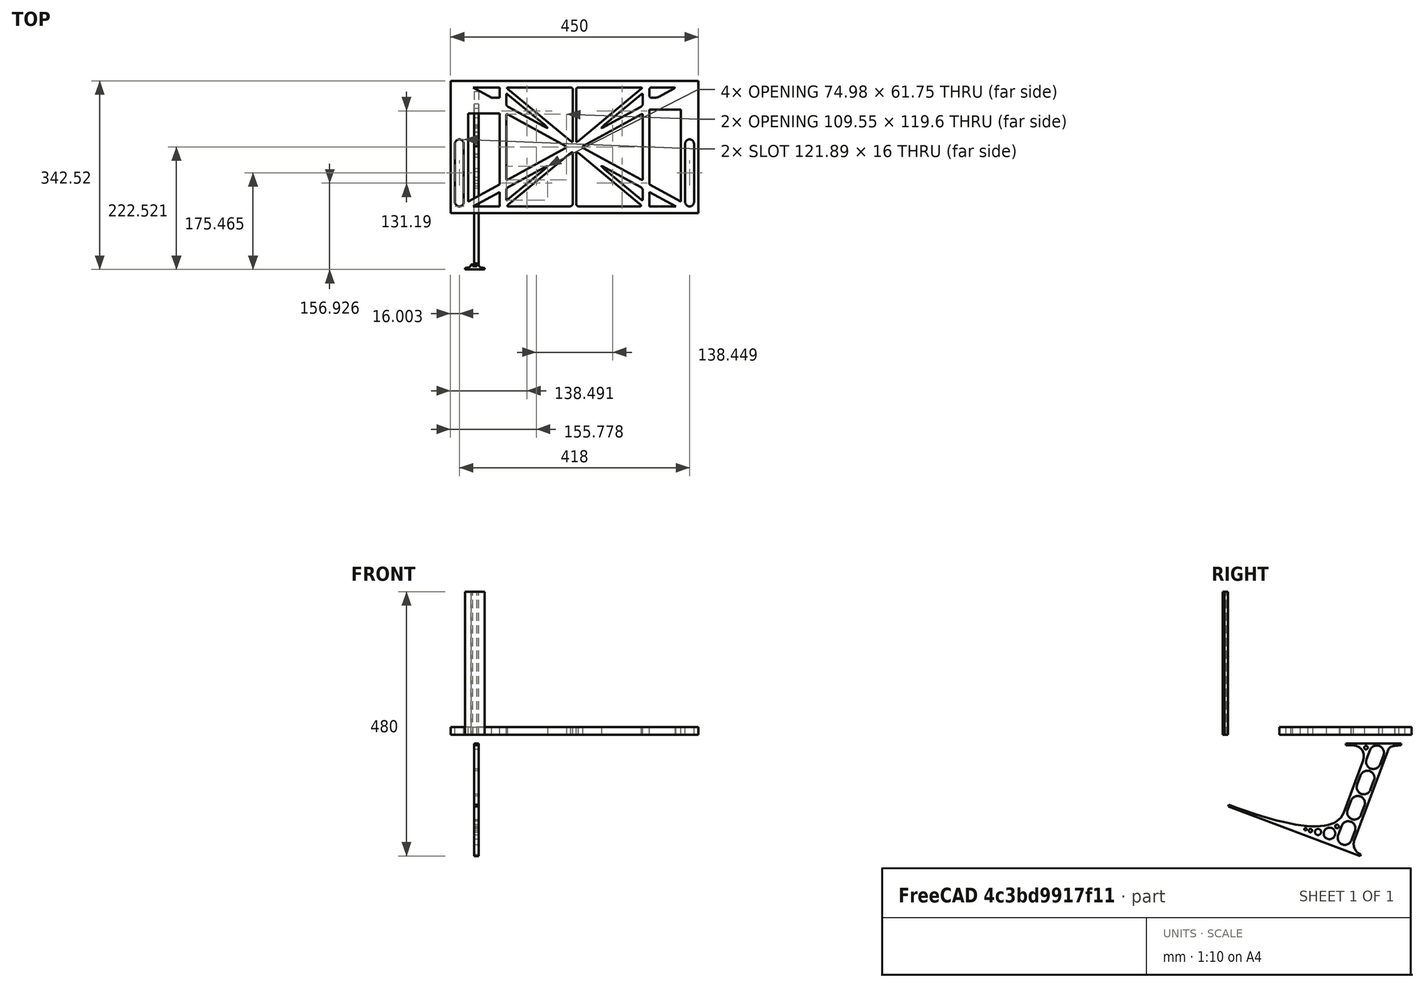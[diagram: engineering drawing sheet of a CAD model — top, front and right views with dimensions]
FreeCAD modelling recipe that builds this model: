
FCSTD DOCUMENT  (FreeCAD 0.19R0.19.2)
Label: laptopStand104
License: All rights reserved
LicenseURL: http://en.wikipedia.org/wiki/All_rights_reserved
objects: Sketcher::SketchObject×3, Part::Extrusion×3
note: 6 computed .brp shape members not serialized (recipe doc carries the construction recipe); baked Part::Feature solids carry a one-line shape summary decoded from their .brp

FEATURE [Sketcher::SketchObject] Sketch
  FullyConstrained = false
  sketch-geometry (294):
    g0: LineSegment StartX=-10.9272 StartY=-82.7794 StartZ=0 EndX=46.0728 EndY=-51.4823 EndZ=0
    g1: LineSegment StartX=366.073 StartY=-91.7794 StartZ=0 EndX=318.073 EndY=-65.424 EndZ=0
    g2: LineSegment StartX=-10.9272 StartY=77.3346 StartZ=0 EndX=-10.9272 EndY=-82.7794 EndZ=0
    g3: LineSegment StartX=375.073 StartY=-82.7896 StartZ=0 EndX=375.073 EndY=83.9235 EndZ=0
    g4: LineSegment StartX=-1.92719 StartY=-91.7794 StartZ=0 EndX=46.0728 EndY=-91.7794 EndZ=0
    g5: LineSegment StartX=318.073 StartY=83.9235 StartZ=0 EndX=318.073 EndY=-51.4823 EndZ=0
    g6: LineSegment StartX=318.073 StartY=-51.4823 StartZ=0 EndX=375.073 EndY=-82.7794 EndZ=0
    g7: LineSegment StartX=318.073 StartY=-65.424 StartZ=0 EndX=318.073 EndY=-91.7794 EndZ=0
    g8: LineSegment StartX=318.073 StartY=-91.7794 StartZ=0 EndX=366.073 EndY=-91.7794 EndZ=0
    g9: LineSegment StartX=46.0728 StartY=-65.424 StartZ=0 EndX=-1.92719 EndY=-91.7794 EndZ=0
    g10: LineSegment StartX=46.0728 StartY=-65.424 StartZ=0 EndX=46.0728 EndY=-91.7794 EndZ=0
    g11: LineSegment StartX=46.0728 StartY=77.3346 StartZ=0 EndX=46.0728 EndY=-51.4823 EndZ=0
    g12: LineSegment StartX=-42.9272 StartY=136.221 StartZ=0 EndX=-42.9272 EndY=-103.779 EndZ=0
    g13: LineSegment StartX=407.073 StartY=136.221 StartZ=0 EndX=407.073 EndY=-103.779 EndZ=0
    g14: ArcOfCircle CenterX=-26.9272 CenterY=22.1087 CenterZ=0 NormalX=0 NormalY=0 NormalZ=1 AngleXU=0 Radius=8 StartAngle=1e-16 EndAngle=3.14159
    g15: ArcOfCircle CenterX=-26.9272 CenterY=-83.7794 CenterZ=0 NormalX=0 NormalY=0 NormalZ=1 AngleXU=0 Radius=8 StartAngle=3.14159 EndAngle=6.28319
    g16: LineSegment StartX=-34.9272 StartY=22.1087 StartZ=0 EndX=-34.9272 EndY=-83.7794 EndZ=0
    g17: LineSegment StartX=-18.9272 StartY=22.1087 StartZ=0 EndX=-18.9272 EndY=-83.7794 EndZ=0
    g18: ArcOfCircle CenterX=391.073 CenterY=22.1087 CenterZ=0 NormalX=0 NormalY=0 NormalZ=1 AngleXU=0 Radius=8 StartAngle=-4.4e-15 EndAngle=3.14159
    g19: LineSegment StartX=399.073 StartY=22.1087 StartZ=0 EndX=399.073 EndY=-83.7794 EndZ=0
    g20: LineSegment StartX=383.073 StartY=22.1087 StartZ=0 EndX=383.073 EndY=-83.7794 EndZ=0
    g21: ArcOfCircle CenterX=391.073 CenterY=-83.7794 CenterZ=0 NormalX=0 NormalY=0 NormalZ=1 AngleXU=0 Radius=8 StartAngle=3.14159 EndAngle=6.28319
    g22: Circle CenterX=175.022 CenterY=27.0628 CenterZ=0 NormalX=0 NormalY=0 NormalZ=1 AngleXU=0 Radius=1
    g23: Circle CenterX=179.022 CenterY=24.8665 CenterZ=0 NormalX=0 NormalY=0 NormalZ=1 AngleXU=0 Radius=1
    g24: Circle CenterX=179.022 CenterY=27.0628 CenterZ=0 NormalX=0 NormalY=0 NormalZ=1 AngleXU=0 Radius=1
    g25: BSplineCurve PolesCount=3 KnotsCount=2 Degree=2 IsPeriodic=0
    g26: GeomPoint X=175.022 Y=27.0628 Z=0
    g27: GeomPoint X=179.022 Y=27.0628 Z=0
    g28: Circle CenterX=189.124 CenterY=27.0628 CenterZ=0 NormalX=0 NormalY=0 NormalZ=1 AngleXU=0 Radius=1
    g29: Circle CenterX=185.124 CenterY=24.8665 CenterZ=0 NormalX=0 NormalY=0 NormalZ=1 AngleXU=0 Radius=1
    g30: Circle CenterX=185.124 CenterY=27.0628 CenterZ=0 NormalX=0 NormalY=0 NormalZ=1 AngleXU=0 Radius=1
    g31: BSplineCurve PolesCount=3 KnotsCount=2 Degree=2 IsPeriodic=0
    g32: GeomPoint X=189.124 Y=27.0628 Z=0
    g33: GeomPoint X=185.124 Y=27.0628 Z=0
    g34: Circle CenterX=175.022 CenterY=5.37834 CenterZ=0 NormalX=0 NormalY=0 NormalZ=1 AngleXU=0 Radius=1
    g35: Circle CenterX=179.022 CenterY=7.57463 CenterZ=0 NormalX=0 NormalY=0 NormalZ=1 AngleXU=0 Radius=1
    g36: Circle CenterX=179.022 CenterY=5.34704 CenterZ=0 NormalX=0 NormalY=0 NormalZ=1 AngleXU=0 Radius=1
    g37: BSplineCurve PolesCount=3 KnotsCount=2 Degree=2 IsPeriodic=0
    g38: GeomPoint X=175.022 Y=5.37834 Z=0
    g39: GeomPoint X=179.022 Y=5.34704 Z=0
    g40: Circle CenterX=189.124 CenterY=5.37834 CenterZ=0 NormalX=0 NormalY=0 NormalZ=1 AngleXU=0 Radius=1
    g41: Circle CenterX=185.124 CenterY=7.57463 CenterZ=0 NormalX=0 NormalY=0 NormalZ=1 AngleXU=0 Radius=1
    g42: Circle CenterX=185.124 CenterY=5.34704 CenterZ=0 NormalX=0 NormalY=0 NormalZ=1 AngleXU=0 Radius=1
    g43: BSplineCurve PolesCount=3 KnotsCount=2 Degree=2 IsPeriodic=0
    g44: GeomPoint X=189.124 Y=5.37834 Z=0
    g45: GeomPoint X=185.124 Y=5.34704 Z=0
    g46: Circle CenterX=165.871 CenterY=18.1458 CenterZ=0 NormalX=0 NormalY=0 NormalZ=1 AngleXU=0 Radius=1
    g47: Circle CenterX=169.377 CenterY=16.2206 CenterZ=0 NormalX=0 NormalY=0 NormalZ=1 AngleXU=0 Radius=1
    g48: Circle CenterX=165.871 CenterY=14.2954 CenterZ=0 NormalX=0 NormalY=0 NormalZ=1 AngleXU=0 Radius=1
    g49: BSplineCurve PolesCount=3 KnotsCount=2 Degree=2 IsPeriodic=0
    g50: GeomPoint X=165.871 Y=18.1458 Z=0
    g51: GeomPoint X=165.871 Y=14.2954 Z=0
    g52: Circle CenterX=198.275 CenterY=18.1458 CenterZ=0 NormalX=0 NormalY=0 NormalZ=1 AngleXU=0 Radius=1
    g53: Circle CenterX=194.768 CenterY=16.2206 CenterZ=0 NormalX=0 NormalY=0 NormalZ=1 AngleXU=0 Radius=1
    g54: Circle CenterX=198.275 CenterY=14.2954 CenterZ=0 NormalX=0 NormalY=0 NormalZ=1 AngleXU=0 Radius=1
    g55: BSplineCurve PolesCount=3 KnotsCount=2 Degree=2 IsPeriodic=0
    g56: GeomPoint X=198.275 Y=18.1458 Z=0
    g57: GeomPoint X=198.275 Y=14.2954 Z=0
    g58: LineSegment StartX=407.073 StartY=-103.779 StartZ=0 EndX=-42.9272 EndY=-103.779 EndZ=0
    g59: LineSegment StartX=407.073 StartY=136.221 StartZ=0 EndX=-42.9272 EndY=136.221 EndZ=0
    g60: LineSegment StartX=46.0728 StartY=77.3346 StartZ=0 EndX=-10.9272 EndY=77.3346 EndZ=0
    g61: LineSegment StartX=46.0728 StartY=105.865 StartZ=0 EndX=31.5028 EndY=105.865 EndZ=0
    g62: LineSegment StartX=46.0728 StartY=124.221 StartZ=0 EndX=46.0728 EndY=105.865 EndZ=0
    g63: LineSegment StartX=-1.92719 StartY=124.221 StartZ=0 EndX=31.5028 EndY=105.865 EndZ=0
    g64: LineSegment StartX=46.0728 StartY=124.221 StartZ=0 EndX=-1.92719 EndY=124.221 EndZ=0
    g65: LineSegment StartX=318.073 StartY=83.9235 StartZ=0 EndX=375.073 EndY=83.9235 EndZ=0
    g66: Circle CenterX=125.607 CenterY=54.1951 CenterZ=0 NormalX=0 NormalY=0 NormalZ=1 AngleXU=0 Radius=1
    g67: Circle CenterX=139.632 CenterY=46.4944 CenterZ=0 NormalX=0 NormalY=0 NormalZ=1 AngleXU=0 Radius=1
    g68: Circle CenterX=127.326 CenterY=56.7187 CenterZ=0 NormalX=0 NormalY=0 NormalZ=1 AngleXU=0 Radius=1
    g69: BSplineCurve PolesCount=3 KnotsCount=2 Degree=2 IsPeriodic=0
    g70: GeomPoint X=125.607 Y=54.1951 Z=0
    g71: GeomPoint X=127.326 Y=56.7187 Z=0
    g72: Circle CenterX=236.821 CenterY=56.7187 CenterZ=0 NormalX=0 NormalY=0 NormalZ=1 AngleXU=0 Radius=1
    g73: Circle CenterX=224.513 CenterY=46.4944 CenterZ=0 NormalX=0 NormalY=0 NormalZ=1 AngleXU=0 Radius=1
    g74: Circle CenterX=238.538 CenterY=54.1951 CenterZ=0 NormalX=0 NormalY=0 NormalZ=1 AngleXU=0 Radius=1
    g75: BSplineCurve PolesCount=3 KnotsCount=2 Degree=2 IsPeriodic=0
    g76: GeomPoint X=236.821 Y=56.7187 Z=0
    g77: GeomPoint X=238.538 Y=54.1951 Z=0
    g78: Circle CenterX=238.538 CenterY=-21.7539 CenterZ=0 NormalX=0 NormalY=0 NormalZ=1 AngleXU=0 Radius=1
    g79: Circle CenterX=224.513 CenterY=-14.0532 CenterZ=0 NormalX=0 NormalY=0 NormalZ=1 AngleXU=0 Radius=1
    g80: Circle CenterX=236.821 CenterY=-24.2775 CenterZ=0 NormalX=0 NormalY=0 NormalZ=1 AngleXU=0 Radius=1
    g81: BSplineCurve PolesCount=3 KnotsCount=2 Degree=2 IsPeriodic=0
    g82: GeomPoint X=238.538 Y=-21.7539 Z=0
    g83: GeomPoint X=236.821 Y=-24.2775 Z=0
    g84: Circle CenterX=125.607 CenterY=-21.7539 CenterZ=0 NormalX=0 NormalY=0 NormalZ=1 AngleXU=0 Radius=1
    g85: Circle CenterX=139.632 CenterY=-14.0532 CenterZ=0 NormalX=0 NormalY=0 NormalZ=1 AngleXU=0 Radius=1
    g86: Circle CenterX=127.325 CenterY=-24.2775 CenterZ=0 NormalX=0 NormalY=0 NormalZ=1 AngleXU=0 Radius=1
    g87: BSplineCurve PolesCount=3 KnotsCount=2 Degree=2 IsPeriodic=0
    g88: GeomPoint X=125.607 Y=-21.7539 Z=0
    g89: GeomPoint X=127.325 Y=-24.2775 Z=0
    g90: Circle CenterX=302.996 CenterY=111.695 CenterZ=0 NormalX=0 NormalY=0 NormalZ=1 AngleXU=0 Radius=1
    g91: Circle CenterX=306.073 CenterY=114.251 CenterZ=0 NormalX=0 NormalY=0 NormalZ=1 AngleXU=0 Radius=1
    g92: Circle CenterX=306.073 CenterY=110.251 CenterZ=0 NormalX=0 NormalY=0 NormalZ=1 AngleXU=0 Radius=1
    g93: BSplineCurve PolesCount=3 KnotsCount=2 Degree=2 IsPeriodic=0
    g94: GeomPoint X=302.996 Y=111.695 Z=0
    g95: GeomPoint X=306.073 Y=110.251 Z=0
    g96: Circle CenterX=306.073 CenterY=95.2763 CenterZ=0 NormalX=0 NormalY=0 NormalZ=1 AngleXU=0 Radius=1
    g97: Circle CenterX=306.073 CenterY=91.2763 CenterZ=0 NormalX=0 NormalY=0 NormalZ=1 AngleXU=0 Radius=1
    g98: Circle CenterX=302.567 CenterY=89.3511 CenterZ=0 NormalX=0 NormalY=0 NormalZ=1 AngleXU=0 Radius=1
    g99: BSplineCurve PolesCount=3 KnotsCount=2 Degree=2 IsPeriodic=0
    g100: GeomPoint X=306.073 Y=95.2763 Z=0
    g101: GeomPoint X=302.567 Y=89.3511 Z=0
    g102: LineSegment StartX=306.073 StartY=110.251 StartZ=0 EndX=306.073 EndY=95.2763 EndZ=0
    g103: LineSegment StartX=302.996 StartY=111.695 StartZ=0 EndX=236.821 EndY=56.7187 EndZ=0
    g104: LineSegment StartX=238.538 StartY=54.1951 StartZ=0 EndX=302.567 EndY=89.3511 EndZ=0
    g105: Circle CenterX=61.1496 CenterY=111.695 CenterZ=0 NormalX=0 NormalY=0 NormalZ=1 AngleXU=0 Radius=1
    g106: Circle CenterX=58.0728 CenterY=114.251 CenterZ=0 NormalX=0 NormalY=0 NormalZ=1 AngleXU=0 Radius=1
    g107: Circle CenterX=58.0728 CenterY=110.251 CenterZ=0 NormalX=0 NormalY=0 NormalZ=1 AngleXU=0 Radius=1
    g108: BSplineCurve PolesCount=3 KnotsCount=2 Degree=2 IsPeriodic=0
    g109: GeomPoint X=61.1496 Y=111.695 Z=0
    g110: GeomPoint X=58.0728 Y=110.251 Z=0
    g111: Circle CenterX=61.5791 CenterY=89.3511 CenterZ=0 NormalX=0 NormalY=0 NormalZ=1 AngleXU=0 Radius=1
    g112: Circle CenterX=58.0728 CenterY=91.2763 CenterZ=0 NormalX=0 NormalY=0 NormalZ=1 AngleXU=0 Radius=1
    g113: Circle CenterX=58.0728 CenterY=95.2763 CenterZ=0 NormalX=0 NormalY=0 NormalZ=1 AngleXU=0 Radius=1
    g114: BSplineCurve PolesCount=3 KnotsCount=2 Degree=2 IsPeriodic=0
    g115: GeomPoint X=61.5791 Y=89.3511 Z=0
    g116: GeomPoint X=58.0728 Y=95.2763 Z=0
    g117: LineSegment StartX=58.0728 StartY=110.251 StartZ=0 EndX=58.0728 EndY=95.2763 EndZ=0
    g118: LineSegment StartX=61.1496 StartY=111.695 StartZ=0 EndX=127.326 EndY=56.7187 EndZ=0
    g119: LineSegment StartX=125.607 StartY=54.1951 StartZ=0 EndX=61.5791 EndY=89.3511 EndZ=0
    g120: Circle CenterX=61.5791 CenterY=-56.9099 CenterZ=0 NormalX=0 NormalY=0 NormalZ=1 AngleXU=0 Radius=1
    g121: Circle CenterX=58.0728 CenterY=-58.8351 CenterZ=0 NormalX=0 NormalY=0 NormalZ=1 AngleXU=0 Radius=1
    g122: Circle CenterX=58.0728 CenterY=-62.8351 CenterZ=0 NormalX=0 NormalY=0 NormalZ=1 AngleXU=0 Radius=1
    g123: BSplineCurve PolesCount=3 KnotsCount=2 Degree=2 IsPeriodic=0
    g124: GeomPoint X=61.5791 Y=-56.9099 Z=0
    g125: GeomPoint X=58.0728 Y=-62.8351 Z=0
    g126: Circle CenterX=58.0728 CenterY=-77.8102 CenterZ=0 NormalX=0 NormalY=0 NormalZ=1 AngleXU=0 Radius=1
    g127: Circle CenterX=58.0728 CenterY=-81.8102 CenterZ=0 NormalX=0 NormalY=0 NormalZ=1 AngleXU=0 Radius=1
    g128: Circle CenterX=61.1496 CenterY=-79.2541 CenterZ=0 NormalX=0 NormalY=0 NormalZ=1 AngleXU=0 Radius=1
    g129: BSplineCurve PolesCount=3 KnotsCount=2 Degree=2 IsPeriodic=0
    g130: GeomPoint X=58.0728 Y=-77.8102 Z=0
    g131: GeomPoint X=61.1496 Y=-79.2541 Z=0
    g132: LineSegment StartX=58.0728 StartY=-62.8351 StartZ=0 EndX=58.0728 EndY=-77.8102 EndZ=0
    g133: LineSegment StartX=61.1496 StartY=-79.2541 StartZ=0 EndX=127.325 EndY=-24.2775 EndZ=0
    g134: LineSegment StartX=125.607 StartY=-21.7539 StartZ=0 EndX=61.5791 EndY=-56.9099 EndZ=0
    g135: Circle CenterX=302.567 CenterY=-56.9099 CenterZ=0 NormalX=0 NormalY=0 NormalZ=1 AngleXU=0 Radius=1
    g136: Circle CenterX=306.073 CenterY=-58.8351 CenterZ=0 NormalX=0 NormalY=0 NormalZ=1 AngleXU=0 Radius=1
    g137: Circle CenterX=306.073 CenterY=-62.8351 CenterZ=0 NormalX=0 NormalY=0 NormalZ=1 AngleXU=0 Radius=1
    g138: BSplineCurve PolesCount=3 KnotsCount=2 Degree=2 IsPeriodic=0
    g139: GeomPoint X=302.567 Y=-56.9099 Z=0
    g140: GeomPoint X=306.073 Y=-62.8351 Z=0
    g141: Circle CenterX=302.996 CenterY=-79.2541 CenterZ=0 NormalX=0 NormalY=0 NormalZ=1 AngleXU=0 Radius=1
    g142: Circle CenterX=306.073 CenterY=-81.8102 CenterZ=0 NormalX=0 NormalY=0 NormalZ=1 AngleXU=0 Radius=1
    g143: Circle CenterX=306.073 CenterY=-77.8102 CenterZ=0 NormalX=0 NormalY=0 NormalZ=1 AngleXU=0 Radius=1
    g144: BSplineCurve PolesCount=3 KnotsCount=2 Degree=2 IsPeriodic=0
    g145: GeomPoint X=302.996 Y=-79.2541 Z=0
    g146: GeomPoint X=306.073 Y=-77.8102 Z=0
    g147: LineSegment StartX=306.073 StartY=-62.8351 StartZ=0 EndX=306.073 EndY=-77.8102 EndZ=0
    g148: LineSegment StartX=302.996 StartY=-79.2541 StartZ=0 EndX=236.821 EndY=-24.2775 EndZ=0
    g149: LineSegment StartX=238.538 StartY=-21.7539 StartZ=0 EndX=302.567 EndY=-56.9099 EndZ=0
    g150: Circle CenterX=61.6457 CenterY=-88.8112 CenterZ=0 NormalX=0 NormalY=0 NormalZ=1 AngleXU=0 Radius=1
    g151: Circle CenterX=58.0728 CenterY=-91.7794 CenterZ=0 NormalX=0 NormalY=0 NormalZ=1 AngleXU=0 Radius=1
    g152: Circle CenterX=63.9135 CenterY=-91.7794 CenterZ=0 NormalX=0 NormalY=0 NormalZ=1 AngleXU=0 Radius=1
    g153: BSplineCurve PolesCount=3 KnotsCount=2 Degree=2 IsPeriodic=0
    g154: GeomPoint X=61.6457 Y=-88.8112 Z=0
    g155: GeomPoint X=63.9135 Y=-91.7794 Z=0
    g156: Circle CenterX=179.022 CenterY=-85.8163 CenterZ=0 NormalX=0 NormalY=0 NormalZ=1 AngleXU=0 Radius=1
    g157: Circle CenterX=179.022 CenterY=-91.7794 CenterZ=0 NormalX=0 NormalY=0 NormalZ=1 AngleXU=0 Radius=1
    g158: Circle CenterX=171.895 CenterY=-91.7794 CenterZ=0 NormalX=0 NormalY=0 NormalZ=1 AngleXU=0 Radius=1
    g159: BSplineCurve PolesCount=3 KnotsCount=2 Degree=2 IsPeriodic=0
    g160: GeomPoint X=179.022 Y=-85.8163 Z=0
    g161: GeomPoint X=171.895 Y=-91.7794 Z=0
    g162: Circle CenterX=185.124 CenterY=-86.2028 CenterZ=0 NormalX=0 NormalY=0 NormalZ=1 AngleXU=0 Radius=1
    g163: Circle CenterX=185.124 CenterY=-91.7794 CenterZ=0 NormalX=0 NormalY=0 NormalZ=1 AngleXU=0 Radius=1
    g164: Circle CenterX=191.747 CenterY=-91.7794 CenterZ=0 NormalX=0 NormalY=0 NormalZ=1 AngleXU=0 Radius=1
    g165: BSplineCurve PolesCount=3 KnotsCount=2 Degree=2 IsPeriodic=0
    g166: GeomPoint X=185.124 Y=-86.2028 Z=0
    g167: GeomPoint X=191.747 Y=-91.7794 Z=0
    g168: Circle CenterX=299.888 CenterY=-86.6413 CenterZ=0 NormalX=0 NormalY=0 NormalZ=1 AngleXU=0 Radius=1
    g169: Circle CenterX=306.073 CenterY=-91.7794 CenterZ=0 NormalX=0 NormalY=0 NormalZ=1 AngleXU=0 Radius=1
    g170: Circle CenterX=298.776 CenterY=-91.7794 CenterZ=0 NormalX=0 NormalY=0 NormalZ=1 AngleXU=0 Radius=1
    g171: BSplineCurve PolesCount=3 KnotsCount=2 Degree=2 IsPeriodic=0
    g172: GeomPoint X=299.888 Y=-86.6413 Z=0
    g173: GeomPoint X=298.776 Y=-91.7794 Z=0
    g174: LineSegment StartX=189.124 StartY=5.37834 StartZ=0 EndX=299.888 EndY=-86.6413 EndZ=0
    g175: LineSegment StartX=298.776 StartY=-91.7794 StartZ=0 EndX=191.747 EndY=-91.7794 EndZ=0
    g176: LineSegment StartX=185.124 StartY=-86.2028 StartZ=0 EndX=185.124 EndY=5.34704 EndZ=0
    g177: LineSegment StartX=179.022 StartY=5.34704 StartZ=0 EndX=179.022 EndY=-85.8163 EndZ=0
    g178: LineSegment StartX=171.895 StartY=-91.7794 StartZ=0 EndX=63.9135 EndY=-91.7794 EndZ=0
    g179: LineSegment StartX=61.6457 StartY=-88.8112 StartZ=0 EndX=175.022 EndY=5.37834 EndZ=0
    g180: Circle CenterX=302.073 CenterY=124.221 CenterZ=0 NormalX=0 NormalY=0 NormalZ=1 AngleXU=0 Radius=1
    g181: Circle CenterX=306.073 CenterY=124.221 CenterZ=0 NormalX=0 NormalY=0 NormalZ=1 AngleXU=0 Radius=1
    g182: Circle CenterX=302.996 CenterY=121.665 CenterZ=0 NormalX=0 NormalY=0 NormalZ=1 AngleXU=0 Radius=1
    g183: BSplineCurve PolesCount=3 KnotsCount=2 Degree=2 IsPeriodic=0
    g184: GeomPoint X=302.073 Y=124.221 Z=0
    g185: GeomPoint X=302.996 Y=121.665 Z=0
    g186: Circle CenterX=189.124 CenterY=124.221 CenterZ=0 NormalX=0 NormalY=0 NormalZ=1 AngleXU=0 Radius=1
    g187: Circle CenterX=185.124 CenterY=124.221 CenterZ=0 NormalX=0 NormalY=0 NormalZ=1 AngleXU=0 Radius=1
    g188: Circle CenterX=185.124 CenterY=120.221 CenterZ=0 NormalX=0 NormalY=0 NormalZ=1 AngleXU=0 Radius=1
    g189: BSplineCurve PolesCount=3 KnotsCount=2 Degree=2 IsPeriodic=0
    g190: GeomPoint X=189.124 Y=124.221 Z=0
    g191: GeomPoint X=185.124 Y=120.221 Z=0
    g192: Circle CenterX=175.022 CenterY=124.221 CenterZ=0 NormalX=0 NormalY=0 NormalZ=1 AngleXU=0 Radius=1
    g193: Circle CenterX=179.022 CenterY=124.221 CenterZ=0 NormalX=0 NormalY=0 NormalZ=1 AngleXU=0 Radius=1
    g194: Circle CenterX=179.022 CenterY=120.221 CenterZ=0 NormalX=0 NormalY=0 NormalZ=1 AngleXU=0 Radius=1
    g195: BSplineCurve PolesCount=3 KnotsCount=2 Degree=2 IsPeriodic=0
    g196: GeomPoint X=175.022 Y=124.221 Z=0
    g197: GeomPoint X=179.022 Y=120.221 Z=0
    g198: Circle CenterX=62.0728 CenterY=124.221 CenterZ=0 NormalX=0 NormalY=0 NormalZ=1 AngleXU=0 Radius=1
    g199: Circle CenterX=58.0728 CenterY=124.221 CenterZ=0 NormalX=0 NormalY=0 NormalZ=1 AngleXU=0 Radius=1
    g200: Circle CenterX=61.1496 CenterY=121.665 CenterZ=0 NormalX=0 NormalY=0 NormalZ=1 AngleXU=0 Radius=1
    g201: BSplineCurve PolesCount=3 KnotsCount=2 Degree=2 IsPeriodic=0
    g202: GeomPoint X=62.0728 Y=124.221 Z=0
    g203: GeomPoint X=61.1496 Y=121.665 Z=0
    g204: LineSegment StartX=62.0728 StartY=124.221 StartZ=0 EndX=175.022 EndY=124.221 EndZ=0
    g205: LineSegment StartX=179.022 StartY=120.221 StartZ=0 EndX=179.022 EndY=27.0628 EndZ=0
    g206: LineSegment StartX=185.124 StartY=27.0628 StartZ=0 EndX=185.124 EndY=120.221 EndZ=0
    g207: LineSegment StartX=189.124 StartY=124.221 StartZ=0 EndX=302.073 EndY=124.221 EndZ=0
    g208: LineSegment StartX=302.996 StartY=121.665 StartZ=0 EndX=189.124 EndY=27.0628 EndZ=0
    g209: LineSegment StartX=175.022 StartY=27.0628 StartZ=0 EndX=61.1496 EndY=121.665 EndZ=0
    g210: Circle CenterX=61.5791 CenterY=75.4095 CenterZ=0 NormalX=0 NormalY=0 NormalZ=1 AngleXU=0 Radius=1
    g211: Circle CenterX=58.0728 CenterY=77.3346 CenterZ=0 NormalX=0 NormalY=0 NormalZ=1 AngleXU=0 Radius=1
    g212: Circle CenterX=58.0728 CenterY=73.3346 CenterZ=0 NormalX=0 NormalY=0 NormalZ=1 AngleXU=0 Radius=1
    g213: BSplineCurve PolesCount=3 KnotsCount=2 Degree=2 IsPeriodic=0
    g214: GeomPoint X=61.5791 Y=75.4095 Z=0
    g215: GeomPoint X=58.0728 Y=73.3346 Z=0
    g216: Circle CenterX=58.0728 CenterY=-40.8935 CenterZ=0 NormalX=0 NormalY=0 NormalZ=1 AngleXU=0 Radius=1
    g217: Circle CenterX=58.0728 CenterY=-44.8935 CenterZ=0 NormalX=0 NormalY=0 NormalZ=1 AngleXU=0 Radius=1
    g218: Circle CenterX=61.5791 CenterY=-42.9683 CenterZ=0 NormalX=0 NormalY=0 NormalZ=1 AngleXU=0 Radius=1
    g219: BSplineCurve PolesCount=3 KnotsCount=2 Degree=2 IsPeriodic=0
    g220: GeomPoint X=58.0728 Y=-40.8935 Z=0
    g221: GeomPoint X=61.5791 Y=-42.9683 Z=0
    g222: LineSegment StartX=61.5791 StartY=-42.9683 StartZ=0 EndX=165.871 EndY=14.2954 EndZ=0
    g223: LineSegment StartX=165.871 StartY=18.1458 StartZ=0 EndX=61.5791 EndY=75.4095 EndZ=0
    g224: LineSegment StartX=58.0728 StartY=73.3346 StartZ=0 EndX=58.0728 EndY=-40.8935 EndZ=0
    g225: Circle CenterX=302.567 CenterY=-42.9683 CenterZ=0 NormalX=0 NormalY=0 NormalZ=1 AngleXU=0 Radius=1
    g226: Circle CenterX=306.073 CenterY=-44.8935 CenterZ=0 NormalX=0 NormalY=0 NormalZ=1 AngleXU=0 Radius=1
    g227: Circle CenterX=306.073 CenterY=-40.8935 CenterZ=0 NormalX=0 NormalY=0 NormalZ=1 AngleXU=0 Radius=1
    g228: BSplineCurve PolesCount=3 KnotsCount=2 Degree=2 IsPeriodic=0
    g229: GeomPoint X=302.567 Y=-42.9683 Z=0
    g230: GeomPoint X=306.073 Y=-40.8935 Z=0
    g231: Circle CenterX=306.073 CenterY=73.3346 CenterZ=0 NormalX=0 NormalY=0 NormalZ=1 AngleXU=0 Radius=1
    g232: Circle CenterX=306.073 CenterY=77.3346 CenterZ=0 NormalX=0 NormalY=0 NormalZ=1 AngleXU=0 Radius=1
    g233: Circle CenterX=302.567 CenterY=75.4095 CenterZ=0 NormalX=0 NormalY=0 NormalZ=1 AngleXU=0 Radius=1
    g234: BSplineCurve PolesCount=3 KnotsCount=2 Degree=2 IsPeriodic=0
    g235: GeomPoint X=306.073 Y=73.3346 Z=0
    g236: GeomPoint X=302.567 Y=75.4095 Z=0
    g237: LineSegment StartX=302.567 StartY=-42.9683 StartZ=0 EndX=198.275 EndY=14.2954 EndZ=0
    g238: LineSegment StartX=198.275 StartY=18.1458 StartZ=0 EndX=302.567 EndY=75.4095 EndZ=0
    g239: LineSegment StartX=306.073 StartY=73.3346 StartZ=0 EndX=306.073 EndY=-40.8935 EndZ=0
    g240: LineSegment StartX=322.073 StartY=105.865 StartZ=0 EndX=328.643 EndY=105.865 EndZ=0
    g241: LineSegment StartX=318.073 StartY=120.221 StartZ=0 EndX=318.073 EndY=109.865 EndZ=0
    g242: LineSegment StartX=336.157 StartY=107.779 StartZ=0 EndX=362.567 EndY=122.294 EndZ=0
    g243: Circle CenterX=362.073 CenterY=124.221 CenterZ=0 NormalX=0 NormalY=0 NormalZ=1 AngleXU=0 Radius=1
    g244: Circle CenterX=366.073 CenterY=124.221 CenterZ=0 NormalX=0 NormalY=0 NormalZ=1 AngleXU=0 Radius=1
    g245: Circle CenterX=362.567 CenterY=122.294 CenterZ=0 NormalX=0 NormalY=0 NormalZ=1 AngleXU=0 Radius=1
    g246: BSplineCurve PolesCount=3 KnotsCount=2 Degree=2 IsPeriodic=0
    g247: GeomPoint X=362.073 Y=124.221 Z=0
    g248: GeomPoint X=362.567 Y=122.294 Z=0
    g249: Circle CenterX=322.073 CenterY=124.221 CenterZ=0 NormalX=0 NormalY=0 NormalZ=1 AngleXU=0 Radius=1
    g250: Circle CenterX=318.073 CenterY=124.221 CenterZ=0 NormalX=0 NormalY=0 NormalZ=1 AngleXU=0 Radius=1
    g251: Circle CenterX=318.073 CenterY=120.221 CenterZ=0 NormalX=0 NormalY=0 NormalZ=1 AngleXU=0 Radius=1
    g252: BSplineCurve PolesCount=3 KnotsCount=2 Degree=2 IsPeriodic=0
    g253: GeomPoint X=322.073 Y=124.221 Z=0
    g254: GeomPoint X=318.073 Y=120.221 Z=0
    g255: Circle CenterX=322.073 CenterY=105.865 CenterZ=0 NormalX=0 NormalY=0 NormalZ=1 AngleXU=0 Radius=1
    g256: Circle CenterX=318.073 CenterY=105.865 CenterZ=0 NormalX=0 NormalY=0 NormalZ=1 AngleXU=0 Radius=1
    g257: Circle CenterX=318.073 CenterY=109.865 CenterZ=0 NormalX=0 NormalY=0 NormalZ=1 AngleXU=0 Radius=1
    g258: BSplineCurve PolesCount=3 KnotsCount=2 Degree=2 IsPeriodic=0
    g259: GeomPoint X=322.073 Y=105.865 Z=0
    g260: GeomPoint X=318.073 Y=109.865 Z=0
    g261: Circle CenterX=336.157 CenterY=107.779 CenterZ=0 NormalX=0 NormalY=0 NormalZ=1 AngleXU=0 Radius=1
    g262: Circle CenterX=332.651 CenterY=105.853 CenterZ=0 NormalX=0 NormalY=0 NormalZ=1 AngleXU=0 Radius=1
    g263: Circle CenterX=328.643 CenterY=105.865 CenterZ=0 NormalX=0 NormalY=0 NormalZ=1 AngleXU=0 Radius=1
    g264: BSplineCurve PolesCount=3 KnotsCount=2 Degree=2 IsPeriodic=0
    g265: GeomPoint X=336.157 Y=107.779 Z=0
    g266: GeomPoint X=328.643 Y=105.865 Z=0
    g267: LineSegment StartX=322.073 StartY=124.221 StartZ=0 EndX=362.073 EndY=124.221 EndZ=0
    g268: LineSegment StartX=318.073 StartY=83.9235 StartZ=0 EndX=322.073 EndY=83.9235 EndZ=0
    g269: LineSegment StartX=318.073 StartY=83.9235 StartZ=0 EndX=318.073 EndY=79.9235 EndZ=0
    g270: LineSegment StartX=375.073 StartY=83.9235 StartZ=0 EndX=371.073 EndY=83.9235 EndZ=0
    g271: LineSegment StartX=375.073 StartY=83.9235 StartZ=0 EndX=375.073 EndY=79.9235 EndZ=0
    g272: LineSegment StartX=375.073 StartY=-82.7896 StartZ=0 EndX=375.073 EndY=-78.7896 EndZ=0
    g273: LineSegment StartX=318.073 StartY=-51.4823 StartZ=0 EndX=321.579 EndY=-53.4075 EndZ=0
    g274: LineSegment StartX=318.073 StartY=-51.4823 StartZ=0 EndX=318.073 EndY=-47.4823 EndZ=0
    g275: LineSegment StartX=375.073 StartY=-82.7896 StartZ=0 EndX=371.567 EndY=-80.8644 EndZ=0
    g276: Circle CenterX=371.567 CenterY=-80.8644 CenterZ=0 NormalX=0 NormalY=0 NormalZ=1 AngleXU=0 Radius=1
    g277: Circle CenterX=375.073 CenterY=-82.7896 CenterZ=0 NormalX=0 NormalY=0 NormalZ=1 AngleXU=0 Radius=1
    g278: Circle CenterX=375.073 CenterY=-78.7896 CenterZ=0 NormalX=0 NormalY=0 NormalZ=1 AngleXU=0 Radius=1
    g279: BSplineCurve PolesCount=3 KnotsCount=2 Degree=2 IsPeriodic=0
    g280: GeomPoint X=371.567 Y=-80.8644 Z=0
    g281: GeomPoint X=375.073 Y=-78.7896 Z=0
    g282: Circle CenterX=321.579 CenterY=-53.4075 CenterZ=0 NormalX=0 NormalY=0 NormalZ=1 AngleXU=0 Radius=1
    g283: Circle CenterX=318.073 CenterY=-51.4823 CenterZ=0 NormalX=0 NormalY=0 NormalZ=1 AngleXU=0 Radius=1
    g284: Circle CenterX=318.073 CenterY=-47.4823 CenterZ=0 NormalX=0 NormalY=0 NormalZ=1 AngleXU=0 Radius=1
    g285: BSplineCurve PolesCount=3 KnotsCount=2 Degree=2 IsPeriodic=0
    g286: GeomPoint X=321.579 Y=-53.4075 Z=0
    g287: GeomPoint X=318.073 Y=-47.4823 Z=0
    g288: Circle CenterX=318.073 CenterY=79.9235 CenterZ=0 NormalX=0 NormalY=0 NormalZ=1 AngleXU=0 Radius=1
    g289: Circle CenterX=318.073 CenterY=83.9235 CenterZ=0 NormalX=0 NormalY=0 NormalZ=1 AngleXU=0 Radius=1
    g290: Circle CenterX=322.073 CenterY=83.9235 CenterZ=0 NormalX=0 NormalY=0 NormalZ=1 AngleXU=0 Radius=1
    g291: BSplineCurve PolesCount=3 KnotsCount=2 Degree=2 IsPeriodic=0
    g292: GeomPoint X=318.073 Y=79.9235 Z=0
    g293: GeomPoint X=322.073 Y=83.9235 Z=0
  constraints (507):
    c: Horizontal(g4)
    c: Coincident(g5,g6)
    c: Coincident(g7,g1)
    c: Tangent(g5,g7)
    c: Coincident(g10,g9)
    c: Coincident(g0,g11)
    c: Block(g6)
    c: Block(g3)
    c: Block(g1)
    c: Block(g7)
    c: Block(g10)
    c: Block(g9)
    c: Block(g0)
    c: Block(g2)
    c: Block(g8)
    c: Block(g4)
    c: Vertical(g12)
    c: Vertical(g13)
    c: Block(g13)
    c: Block(g12)
    c: Tangent(g14,g17) = 1.5708
    c: Tangent(g14,g16) = -1.5708
    c: Tangent(g16,g15) = -1.5708
    c: Tangent(g17,g15) = 1.5708
    c: Vertical(g16)
    c: Equal(g14,g15)
    c: Block(g17)
    c: Block(g16)
    c: Tangent(g18,g19) = 1.5708
    c: Tangent(g19,g21) = 1.5708
    c: Equal(g18,g21)
    c: Coincident(g20,g18)
    c: Coincident(g20,g21)
    c: Block(g19)
    c: Block(g20)
    c: Weight(g22) = 1
    c: Equal(g22,g23)
    c: Equal(g22,g24)
    c: InternalAlignment(g22,g25)
    c: InternalAlignment(g23,g25)
    c: InternalAlignment(g24,g25)
    c: InternalAlignment(g26,g25)
    c: InternalAlignment(g27,g25)
    c: Weight(g28) = 1
    c: Equal(g28,g29)
    c: Equal(g28,g30)
    c: InternalAlignment(g28,g31)
    c: InternalAlignment(g29,g31)
    c: InternalAlignment(g30,g31)
    c: InternalAlignment(g32,g31)
    c: InternalAlignment(g33,g31)
    c: Block(g31)
    c: Block(g25)
    c: Weight(g34) = 1
    c: Equal(g34,g35)
    c: Equal(g34,g36)
    c: InternalAlignment(g34,g37)
    c: InternalAlignment(g35,g37)
    c: InternalAlignment(g36,g37)
    c: InternalAlignment(g38,g37)
    c: InternalAlignment(g39,g37)
    c: Weight(g40) = 1
    c: Equal(g40,g41)
    c: Equal(g40,g42)
    c: InternalAlignment(g40,g43)
    c: InternalAlignment(g41,g43)
    c: InternalAlignment(g42,g43)
    c: InternalAlignment(g44,g43)
    c: InternalAlignment(g45,g43)
    c: Block(g43)
    c: Block(g37)
    c: Weight(g46) = 1
    c: Equal(g46,g47)
    c: Equal(g46,g48)
    c: InternalAlignment(g46,g49)
    c: InternalAlignment(g47,g49)
    c: InternalAlignment(g48,g49)
    c: InternalAlignment(g50,g49)
    c: InternalAlignment(g51,g49)
    c: Weight(g52) = 1
    c: Equal(g52,g53)
    c: Equal(g52,g54)
    c: InternalAlignment(g52,g55)
    c: InternalAlignment(g53,g55)
    c: InternalAlignment(g54,g55)
    c: InternalAlignment(g56,g55)
    c: InternalAlignment(g57,g55)
    c: Block(g49)
    c: Block(g55)
    c: Coincident(g58,g13)
    c: Coincident(g58,g12)
    c: Horizontal(g58)
    c: Distance(g58) = 450
    c: Coincident(g59,g13)
    c: Coincident(g59,g12)
    c: Horizontal(g59)
    c: Horizontal(g60)
    c: Coincident(g11,g60)
    c: Horizontal(g61)
    c: Vertical(g62)
    c: Block(g62)
    c: Block(g61)
    c: Block(g60)
    c: Distance(g62) = 18.3554
    c: Coincident(g64,g62)
    c: Coincident(g64,g63)
    c: Horizontal(g64)
    c: Block(g64)
    c: Block(g63)
    c: Coincident(g61,g63)
    c: Coincident(g2,g60)
    c: Coincident(g65,g5)
    c: Horizontal(g65)
    c: Block(g65)
    c: Coincident(g3,g65)
    c: Weight(g66) = 1
    c: Equal(g66,g67)
    c: Equal(g66,g68)
    c: InternalAlignment(g66,g69)
    c: InternalAlignment(g67,g69)
    c: InternalAlignment(g68,g69)
    c: InternalAlignment(g70,g69)
    c: InternalAlignment(g71,g69)
    c: Block(g69)
    c: Weight(g72) = 1
    c: Equal(g72,g73)
    c: Equal(g72,g74)
    c: InternalAlignment(g72,g75)
    c: InternalAlignment(g73,g75)
    c: InternalAlignment(g74,g75)
    c: InternalAlignment(g76,g75)
    c: InternalAlignment(g77,g75)
    c: Block(g75)
    c: Weight(g78) = 1
    c: Equal(g78,g79)
    c: Equal(g78,g80)
    c: InternalAlignment(g78,g81)
    c: InternalAlignment(g79,g81)
    c: InternalAlignment(g80,g81)
    c: InternalAlignment(g82,g81)
    c: InternalAlignment(g83,g81)
    c: Block(g81)
    c: Weight(g84) = 1
    c: Equal(g84,g85)
    c: Equal(g84,g86)
    c: InternalAlignment(g84,g87)
    c: InternalAlignment(g85,g87)
    c: InternalAlignment(g86,g87)
    c: InternalAlignment(g88,g87)
    c: InternalAlignment(g89,g87)
    c: Block(g87)
    c: Weight(g90) = 1
    c: Equal(g90,g91)
    c: Equal(g90,g92)
    c: InternalAlignment(g90,g93)
    c: InternalAlignment(g91,g93)
    c: InternalAlignment(g92,g93)
    c: InternalAlignment(g94,g93)
    c: InternalAlignment(g95,g93)
    c: Weight(g96) = 1
    c: Equal(g96,g97)
    c: Equal(g96,g98)
    c: InternalAlignment(g96,g99)
    c: InternalAlignment(g97,g99)
    c: InternalAlignment(g98,g99)
    c: InternalAlignment(g100,g99)
    c: InternalAlignment(g101,g99)
    c: Block(g93)
    c: Block(g99)
    c: Coincident(g102,g93)
    c: Coincident(g102,g99)
    c: Vertical(g102)
    c: Coincident(g103,g93)
    c: Coincident(g103,g75)
    c: Coincident(g104,g75)
    c: Coincident(g104,g99)
    c: Weight(g105) = 1
    c: Equal(g105,g106)
    c: Equal(g105,g107)
    c: InternalAlignment(g105,g108)
    c: InternalAlignment(g106,g108)
    c: InternalAlignment(g107,g108)
    c: InternalAlignment(g109,g108)
    c: InternalAlignment(g110,g108)
    c: Weight(g111) = 1
    c: Equal(g111,g112)
    c: Equal(g111,g113)
    c: InternalAlignment(g111,g114)
    c: InternalAlignment(g112,g114)
    c: InternalAlignment(g113,g114)
    c: InternalAlignment(g115,g114)
    c: InternalAlignment(g116,g114)
    c: Block(g108)
    c: Block(g114)
    c: Coincident(g117,g108)
    c: Coincident(g117,g114)
    c: Vertical(g117)
    c: Coincident(g118,g108)
    c: Coincident(g118,g69)
    c: Coincident(g119,g69)
    c: Coincident(g119,g114)
    c: Weight(g120) = 1
    c: Equal(g120,g121)
    c: Equal(g120,g122)
    c: InternalAlignment(g120,g123)
    c: InternalAlignment(g121,g123)
    c: InternalAlignment(g122,g123)
    c: InternalAlignment(g124,g123)
    c: InternalAlignment(g125,g123)
    c: Weight(g126) = 1
    c: Equal(g126,g127)
    c: Equal(g126,g128)
    c: InternalAlignment(g126,g129)
    c: InternalAlignment(g127,g129)
    c: InternalAlignment(g128,g129)
    c: InternalAlignment(g130,g129)
    c: InternalAlignment(g131,g129)
    c: Block(g123)
    c: Block(g129)
    c: Coincident(g132,g123)
    c: Coincident(g132,g129)
    c: Vertical(g132)
    c: Coincident(g133,g129)
    c: Coincident(g133,g87)
    c: Coincident(g134,g87)
    c: Coincident(g134,g123)
    c: Weight(g135) = 1
    c: Equal(g135,g136)
    c: Equal(g135,g137)
    c: InternalAlignment(g135,g138)
    c: InternalAlignment(g136,g138)
    c: InternalAlignment(g137,g138)
    c: InternalAlignment(g139,g138)
    c: InternalAlignment(g140,g138)
    c: Weight(g141) = 1
    c: Equal(g141,g142)
    c: Equal(g141,g143)
    c: InternalAlignment(g141,g144)
    c: InternalAlignment(g142,g144)
    c: InternalAlignment(g143,g144)
    c: InternalAlignment(g145,g144)
    c: InternalAlignment(g146,g144)
    c: Block(g138)
    c: Block(g144)
    c: Coincident(g147,g138)
    c: Coincident(g147,g144)
    c: Vertical(g147)
    c: Coincident(g148,g144)
    c: Coincident(g148,g81)
    c: Coincident(g149,g81)
    c: Coincident(g149,g138)
    c: Weight(g150) = 1
    c: Equal(g150,g151)
    c: Equal(g150,g152)
    c: InternalAlignment(g150,g153)
    c: InternalAlignment(g151,g153)
    c: InternalAlignment(g152,g153)
    c: InternalAlignment(g154,g153)
    c: InternalAlignment(g155,g153)
    c: Weight(g156) = 1
    c: Equal(g156,g157)
    c: Equal(g156,g158)
    c: InternalAlignment(g156,g159)
    c: InternalAlignment(g157,g159)
    c: InternalAlignment(g158,g159)
    c: InternalAlignment(g160,g159)
    c: InternalAlignment(g161,g159)
    c: Weight(g162) = 1
    c: Equal(g162,g163)
    c: Equal(g162,g164)
    c: InternalAlignment(g162,g165)
    c: InternalAlignment(g163,g165)
    c: InternalAlignment(g164,g165)
    c: InternalAlignment(g166,g165)
    c: InternalAlignment(g167,g165)
    c: Weight(g168) = 1
    c: Equal(g168,g169)
    c: Equal(g168,g170)
    c: InternalAlignment(g168,g171)
    c: InternalAlignment(g169,g171)
    c: InternalAlignment(g170,g171)
    c: InternalAlignment(g172,g171)
    c: InternalAlignment(g173,g171)
    c: Block(g171)
    c: Block(g165)
    c: Block(g159)
    c: Block(g153)
    c: Coincident(g174,g43)
    c: Coincident(g174,g171)
    c: Coincident(g175,g171)
    c: Coincident(g175,g165)
    c: Horizontal(g175)
    c: Coincident(g176,g165)
    c: Coincident(g176,g43)
    c: Vertical(g176)
    c: Coincident(g177,g37)
    c: Coincident(g177,g159)
    c: Vertical(g177)
    c: Coincident(g178,g159)
    c: Coincident(g178,g153)
    c: Horizontal(g178)
    c: Coincident(g179,g153)
    c: Coincident(g179,g37)
    c: Weight(g180) = 1
    c: Equal(g180,g181)
    c: Equal(g180,g182)
    c: InternalAlignment(g180,g183)
    c: InternalAlignment(g181,g183)
    c: InternalAlignment(g182,g183)
    c: InternalAlignment(g184,g183)
    c: InternalAlignment(g185,g183)
    c: Weight(g186) = 1
    c: Equal(g186,g187)
    c: Equal(g186,g188)
    c: InternalAlignment(g186,g189)
    c: InternalAlignment(g187,g189)
    c: InternalAlignment(g188,g189)
    c: InternalAlignment(g190,g189)
    c: InternalAlignment(g191,g189)
    c: Weight(g192) = 1
    c: Equal(g192,g193)
    c: Equal(g192,g194)
    c: InternalAlignment(g192,g195)
    c: InternalAlignment(g193,g195)
    c: InternalAlignment(g194,g195)
    c: InternalAlignment(g196,g195)
    c: InternalAlignment(g197,g195)
    c: Weight(g198) = 1
    c: Equal(g198,g199)
    c: Equal(g198,g200)
    c: InternalAlignment(g198,g201)
    c: InternalAlignment(g199,g201)
    c: InternalAlignment(g200,g201)
    c: InternalAlignment(g202,g201)
    c: InternalAlignment(g203,g201)
    c: Block(g201)
    c: Block(g195)
    c: Block(g189)
    c: Block(g183)
    c: Coincident(g204,g201)
    c: Coincident(g204,g195)
    c: Horizontal(g204)
    c: Coincident(g205,g195)
    c: Coincident(g205,g25)
    c: Vertical(g205)
    c: Coincident(g206,g31)
    c: Coincident(g206,g189)
    c: Vertical(g206)
    c: Coincident(g207,g189)
    c: Coincident(g207,g183)
    c: Horizontal(g207)
    c: Coincident(g208,g183)
    c: Coincident(g208,g31)
    c: Coincident(g209,g25)
    c: Weight(g210) = 1
    c: Equal(g210,g211)
    c: Equal(g210,g212)
    c: InternalAlignment(g210,g213)
    c: InternalAlignment(g211,g213)
    c: InternalAlignment(g212,g213)
    c: InternalAlignment(g214,g213)
    c: InternalAlignment(g215,g213)
    c: Weight(g216) = 1
    c: Equal(g216,g217)
    c: Equal(g216,g218)
    c: InternalAlignment(g216,g219)
    c: InternalAlignment(g217,g219)
    c: InternalAlignment(g218,g219)
    c: InternalAlignment(g220,g219)
    c: InternalAlignment(g221,g219)
    c: Block(g219)
    c: Block(g213)
    c: Coincident(g222,g219)
    c: Coincident(g222,g49)
    c: Coincident(g223,g49)
    c: Coincident(g223,g213)
    c: Coincident(g224,g213)
    c: Coincident(g224,g219)
    c: Vertical(g224)
    c: Weight(g225) = 1
    c: Equal(g225,g226)
    c: Equal(g225,g227)
    c: InternalAlignment(g225,g228)
    c: InternalAlignment(g226,g228)
    c: InternalAlignment(g227,g228)
    c: InternalAlignment(g229,g228)
    c: InternalAlignment(g230,g228)
    c: Weight(g231) = 1
    c: Equal(g231,g232)
    c: Equal(g231,g233)
    c: InternalAlignment(g231,g234)
    c: InternalAlignment(g232,g234)
    c: InternalAlignment(g233,g234)
    c: InternalAlignment(g235,g234)
    c: InternalAlignment(g236,g234)
    c: Block(g234)
    c: Block(g228)
    c: Coincident(g237,g228)
    c: Coincident(g237,g55)
    c: Coincident(g238,g55)
    c: Coincident(g238,g234)
    c: Coincident(g239,g234)
    c: Coincident(g239,g228)
    c: Vertical(g239)
    c: Horizontal(g240)
    c: Block(g240)
    c: Vertical(g241)
    c: Block(g241)
    c: Block(g242)
    c: Weight(g243) = 1
    c: Equal(g243,g244)
    c: Equal(g243,g245)
    c: InternalAlignment(g243,g246)
    c: InternalAlignment(g244,g246)
    c: InternalAlignment(g245,g246)
    c: InternalAlignment(g247,g246)
    c: InternalAlignment(g248,g246)
    c: Weight(g249) = 1
    c: Equal(g249,g250)
    c: Equal(g249,g251)
    c: InternalAlignment(g249,g252)
    c: InternalAlignment(g250,g252)
    c: InternalAlignment(g251,g252)
    c: InternalAlignment(g253,g252)
    c: InternalAlignment(g254,g252)
    c: Weight(g255) = 1
    c: Equal(g255,g256)
    c: Equal(g255,g257)
    c: InternalAlignment(g255,g258)
    c: InternalAlignment(g256,g258)
    c: InternalAlignment(g257,g258)
    c: InternalAlignment(g259,g258)
    c: InternalAlignment(g260,g258)
    c: Weight(g261) = 1
    c: Equal(g261,g262)
    c: Equal(g261,g263)
    c: InternalAlignment(g261,g264)
    c: InternalAlignment(g262,g264)
    c: InternalAlignment(g263,g264)
    c: InternalAlignment(g265,g264)
    c: InternalAlignment(g266,g264)
    c: Block(g246)
    c: Block(g252)
    c: Block(g258)
    c: Block(g264)
    c: Coincident(g267,g252)
    c: Coincident(g267,g246)
    c: Horizontal(g267)
    c: Block(g209)
    c: Horizontal(g268)
    c: Vertical(g269)
    c: Horizontal(g270)
    c: Vertical(g271)
    c: Vertical(g272)
    c: Vertical(g274)
    c: Parallel(g6,g273)
    c: Distance(g272) = 4
    c: Distance(g273) = 4
    c: Distance(g274) = 4
    c: Distance(g269) = 4
    c: Distance(g268) = 4
    c: Distance(g271) = 4
    c: Distance(g270) = 4
    c: Coincident(g271,g3)
    c: Coincident(g270,g3)
    c: Coincident(g268,g5)
    c: Coincident(g269,g5)
    c: Coincident(g273,g5)
    c: Coincident(g274,g5)
    c: Coincident(g272,g3)
    c: Distance(g3) = 166.713
    c: Coincident(g275,g3)
    c: Distance(g275) = 4
    c: Parallel(g6,g275)
    c: Coincident(g279,g275)
    c: Weight(g276) = 1
    c: Equal(g276,g277)
    c: Coincident(g277,g3)
    c: Equal(g276,g278)
    c: Coincident(g279,g272)
    c: InternalAlignment(g276,g279)
    c: InternalAlignment(g277,g279)
    c: InternalAlignment(g278,g279)
    c: InternalAlignment(g280,g279)
    c: InternalAlignment(g281,g279)
    c: Coincident(g285,g273)
    c: Weight(g282) = 1
    c: Equal(g282,g283)
    c: Coincident(g283,g5)
    c: Equal(g282,g284)
    c: Coincident(g285,g274)
    c: InternalAlignment(g282,g285)
    c: InternalAlignment(g283,g285)
    c: InternalAlignment(g284,g285)
    c: InternalAlignment(g286,g285)
    c: InternalAlignment(g287,g285)
    c: Coincident(g291,g269)
    c: Weight(g288) = 1
    c: Equal(g288,g289)
    c: Coincident(g289,g5)
    c: Equal(g288,g290)
    c: Coincident(g291,g268)
    c: InternalAlignment(g288,g291)
    c: InternalAlignment(g289,g291)
    c: InternalAlignment(g290,g291)
    c: InternalAlignment(g292,g291)
    c: InternalAlignment(g293,g291)
FEATURE [Sketcher::SketchObject] Sketch001
  FullyConstrained = true
  MapMode = 4
  Placement = pos=(0,0,0) rot=(0.57735,0.57735,0.57735;2.0944rad)
  Support = -> [Sketch]
  sketch-geometry (46):
    g0: BSplineCurve PolesCount=3 KnotsCount=2 Degree=2 IsPeriodic=0
    g1: ArcOfCircle CenterX=73.1223 CenterY=-32.291 CenterZ=0 NormalX=0 NormalY=0 NormalZ=1 AngleXU=0 Radius=13 StartAngle=5.92268 EndAngle=9.06428
    g2: ArcOfCircle CenterX=66.7816 CenterY=-49.1439 CenterZ=0 NormalX=0 NormalY=0 NormalZ=1 AngleXU=0 Radius=13 StartAngle=2.78068 EndAngle=5.92131
    g3: ArcOfCircle CenterX=55.9263 CenterY=-78.1807 CenterZ=0 NormalX=0 NormalY=0 NormalZ=1 AngleXU=0 Radius=13 StartAngle=5.92268 EndAngle=9.06428
    g4: ArcOfCircle CenterX=49.5884 CenterY=-95.0342 CenterZ=0 NormalX=0 NormalY=0 NormalZ=1 AngleXU=0 Radius=13 StartAngle=2.78068 EndAngle=5.92131
    g5: ArcOfCircle CenterX=38.7206 CenterY=-124.067 CenterZ=0 NormalX=0 NormalY=0 NormalZ=1 AngleXU=0 Radius=13 StartAngle=5.92268 EndAngle=9.06428
    g6: ArcOfCircle CenterX=32.3875 CenterY=-140.92 CenterZ=0 NormalX=0 NormalY=0 NormalZ=1 AngleXU=0 Radius=13 StartAngle=2.78068 EndAngle=5.92131
    g7: ArcOfCircle CenterX=21.4715 CenterY=-169.934 CenterZ=0 NormalX=0 NormalY=0 NormalZ=1 AngleXU=0 Radius=13 StartAngle=5.92268 EndAngle=9.06428
    g8: ArcOfCircle CenterX=15.1336 CenterY=-186.787 CenterZ=0 NormalX=0 NormalY=0 NormalZ=1 AngleXU=0 Radius=13 StartAngle=2.78068 EndAngle=5.92131
    g9-g12: Circle x4 (B-spline internal-alignment scaffolding for g13; pole/knot coordinates omitted)
    g13: BSplineCurve PolesCount=4 KnotsCount=2 Degree=3 IsPeriodic=0
    g14: GeomPoint X=28.8094 Y=-19.0875 Z=0
    g15: GeomPoint X=47.0443 Y=-50.4712 Z=0
    g16: Circle CenterX=53.5586 CenterY=-23.2695 CenterZ=0 NormalX=0 NormalY=0 NormalZ=1 AngleXU=0 Radius=3.24518
    g17: Circle CenterX=-195.441 CenterY=-127.082 CenterZ=0 NormalX=0 NormalY=0 NormalZ=1 AngleXU=0 Radius=1
    g18: Circle CenterX=-8.24091 CenterY=-197.481 CenterZ=0 NormalX=0 NormalY=0 NormalZ=1 AngleXU=0 Radius=1
    g19: Circle CenterX=12.8789 CenterY=-141.321 CenterZ=0 NormalX=0 NormalY=0 NormalZ=1 AngleXU=0 Radius=1
    g20: BSplineCurve PolesCount=3 KnotsCount=2 Degree=2 IsPeriodic=0
    g21: GeomPoint X=-195.441 Y=-127.082 Z=0
    g22: GeomPoint X=12.8789 Y=-141.321 Z=0
    g23: Circle CenterX=-12.8016 CenterY=-179.036 CenterZ=0 NormalX=0 NormalY=0 NormalZ=1 AngleXU=0 Radius=10.5072
    g24: Circle CenterX=0.933922 CenterY=-166.43 CenterZ=0 NormalX=0 NormalY=0 NormalZ=1 AngleXU=0 Radius=3.26661
    g25: Circle CenterX=-33.5518 CenterY=-176.44 CenterZ=0 NormalX=0 NormalY=0 NormalZ=1 AngleXU=0 Radius=5.64388
    g26: Circle CenterX=-47.2366 CenterY=-173.859 CenterZ=0 NormalX=0 NormalY=0 NormalZ=1 AngleXU=0 Radius=3.01653
    g27: Circle CenterX=-56.2595 CenterY=-171.456 CenterZ=0 NormalX=0 NormalY=0 NormalZ=1 AngleXU=0 Radius=2.12826
    g28: ArcOfCircle CenterX=51.2151 CenterY=-198.473 CenterZ=0 NormalX=0 NormalY=0 NormalZ=1 AngleXU=0 Radius=20 StartAngle=2.78189 EndAngle=4.35269
    g29: LineSegment StartX=32.4951 StartY=-191.433 StartZ=0 EndX=94.6578 EndY=-26.1352 EndZ=0
    g30: LineSegment StartX=43.1192 StartY=-220.001 StartZ=0 EndX=-196.497 EndY=-129.89 EndZ=0
    g31: LineSegment StartX=43.1192 StartY=-220.001 StartZ=0 EndX=44.1752 EndY=-217.193 EndZ=0
    g32: LineSegment StartX=117.223 StartY=-19.0875 StartZ=0 EndX=117.223 EndY=-16.0875 EndZ=0
    g33: LineSegment StartX=117.223 StartY=-16.0875 StartZ=0 EndX=17.2232 EndY=-16.0875 EndZ=0
    g34: LineSegment StartX=17.2232 StartY=-16.0875 StartZ=0 EndX=17.2232 EndY=-19.0875 EndZ=0
    g35: LineSegment StartX=28.8094 StartY=-19.0875 StartZ=0 EndX=17.2232 EndY=-19.0875 EndZ=0
    g36: LineSegment StartX=47.0443 StartY=-50.4712 StartZ=0 EndX=12.8789 EndY=-141.321 EndZ=0
    g37: LineSegment StartX=-195.441 StartY=-127.082 StartZ=0 EndX=-196.497 EndY=-129.89 EndZ=0
    g38: LineSegment StartX=85.2866 StartY=-36.8766 StartZ=0 EndX=78.9396 EndY=-53.7463 EndZ=0
    g39: LineSegment StartX=60.9579 StartY=-27.7053 StartZ=0 EndX=54.6191 EndY=-44.5532 EndZ=0
    g40: LineSegment StartX=68.0907 StartY=-82.7664 StartZ=0 EndX=61.7465 EndY=-99.6365 EndZ=0
    g41: LineSegment StartX=43.7619 StartY=-73.595 StartZ=0 EndX=37.426 EndY=-90.4435 EndZ=0
    g42: LineSegment StartX=50.885 StartY=-128.652 StartZ=0 EndX=44.5456 EndY=-145.522 EndZ=0
    g43: LineSegment StartX=26.5562 StartY=-119.481 StartZ=0 EndX=20.2251 EndY=-136.329 EndZ=0
    g44: LineSegment StartX=9.3071 StartY=-165.349 StartZ=0 EndX=2.97115 EndY=-182.197 EndZ=0
    g45: LineSegment StartX=33.6358 StartY=-174.52 StartZ=0 EndX=27.2917 EndY=-191.39 EndZ=0
  constraints (71):
    c: Block(g0)
    c: Block(g1)
    c: Block(g2)
    c: Block(g4)
    c: Block(g3)
    c: Block(g6)
    c: Block(g5)
    c: Block(g8)
    c: Block(g7)
    c: Weight(g9) = 1
    c: Equal(g9,g10)
    c: Equal(g9,g11)
    c: Equal(g9,g12)
    c: InternalAlignment(g9-g12 -> g13) x4
    c: InternalAlignment(g14,g13)
    c: InternalAlignment(g15,g13)
    c: Block(g16)
    c: Weight(g17) = 1
    c: Equal(g17,g18)
    c: Equal(g17,g19)
    c: InternalAlignment(g17,g20)
    c: InternalAlignment(g18,g20)
    c: InternalAlignment(g19,g20)
    c: InternalAlignment(g21,g20)
    c: InternalAlignment(g22,g20)
    c: Block(g20)
    c: Block(g23)
    c: Block(g24)
    c: Block(g25)
    c: Block(g26)
    c: Block(g27)
    c: Block(g28)
    c: Coincident(g29,g28)
    c: Coincident(g29,g0)
    c: Block(g13)
    c: Coincident(g31,g30)
    c: Coincident(g31,g28)
    c: Block(g31)
    c: Coincident(g32,g0)
    c: Vertical(g32)
    c: Coincident(g33,g32)
    c: Horizontal(g33)
    c: Coincident(g34,g33)
    c: Vertical(g34)
    c: Block(g33)
    c: Coincident(g35,g13)
    c: Coincident(g35,g34)
    c: Horizontal(g35)
    c: Coincident(g36,g13)
    c: Coincident(g36,g20)
    c: Coincident(g37,g20)
    c: Coincident(g37,g30)
    c: Block(g30)
    c: Coincident(g38,g1)
    c: Coincident(g38,g2)
    c: Coincident(g39,g1)
    c: Coincident(g39,g2)
    c: Coincident(g40,g3)
    c: Coincident(g40,g4)
    c: Coincident(g41,g3)
    c: Coincident(g41,g4)
    c: Coincident(g42,g5)
    c: Coincident(g42,g6)
    c: Coincident(g43,g5)
    c: Coincident(g43,g6)
    c: Coincident(g44,g7)
    c: Coincident(g44,g8)
    c: Coincident(g45,g7)
    c: Coincident(g45,g8)
    c: Distance(g30) = 256
    c: Distance(g33) = 100
FEATURE [Part::Extrusion] Extrude002
  Base = -> Sketch001
  Dir = (1,0,0)
  DirMode = 2
  FaceMakerClass = Part::FaceMakerBullseye
  LengthFwd = 8
  LengthRev = 0
  Solid = true
  Symmetric = false
FEATURE [Sketcher::SketchObject] Sketch002
  FullyConstrained = true
  sketch-geometry (20):
    g0: LineSegment StartX=-2.77179 StartY=-200.304 StartZ=0 EndX=5.22821 EndY=-200.304 EndZ=0
    g1: LineSegment StartX=5.22821 StartY=-200.304 StartZ=0 EndX=5.22821 EndY=-197.304 EndZ=0
    g2: LineSegment StartX=-2.77179 StartY=-200.304 StartZ=0 EndX=-2.77179 EndY=-197.304 EndZ=0
    g3: LineSegment StartX=5.22821 StartY=-197.304 StartZ=0 EndX=8.22821 EndY=-197.304 EndZ=0
    g4: LineSegment StartX=-2.77179 StartY=-197.304 StartZ=0 EndX=-5.77179 EndY=-197.304 EndZ=0
    g5: LineSegment StartX=19.2282 StartY=-203.304 StartZ=0 EndX=19.2282 EndY=-206.304 EndZ=0
    g6: LineSegment StartX=-16.7718 StartY=-203.304 StartZ=0 EndX=-16.7718 EndY=-206.304 EndZ=0
    g7: LineSegment StartX=-16.7718 StartY=-206.304 StartZ=0 EndX=19.2282 EndY=-206.304 EndZ=0
    g8: Circle CenterX=-16.7718 CenterY=-203.304 CenterZ=0 NormalX=0 NormalY=0 NormalZ=1 AngleXU=0 Radius=1
    g9: Circle CenterX=-5.77179 CenterY=-203.304 CenterZ=0 NormalX=0 NormalY=0 NormalZ=1 AngleXU=0 Radius=1
    g10: Circle CenterX=-5.77179 CenterY=-197.304 CenterZ=0 NormalX=0 NormalY=0 NormalZ=1 AngleXU=0 Radius=1
    g11: BSplineCurve PolesCount=3 KnotsCount=2 Degree=2 IsPeriodic=0
    g12: GeomPoint X=-16.7718 Y=-203.304 Z=0
    g13: GeomPoint X=-5.77179 Y=-197.304 Z=0
    g14: Circle CenterX=19.2282 CenterY=-203.304 CenterZ=0 NormalX=0 NormalY=0 NormalZ=1 AngleXU=0 Radius=1
    g15: Circle CenterX=8.22821 CenterY=-203.304 CenterZ=0 NormalX=0 NormalY=0 NormalZ=1 AngleXU=0 Radius=1
    g16: Circle CenterX=8.22821 CenterY=-197.304 CenterZ=0 NormalX=0 NormalY=0 NormalZ=1 AngleXU=0 Radius=1
    g17: BSplineCurve PolesCount=3 KnotsCount=2 Degree=2 IsPeriodic=0
    g18: GeomPoint X=19.2282 Y=-203.304 Z=0
    g19: GeomPoint X=8.22821 Y=-197.304 Z=0
  constraints (41):
    c: Horizontal(g0)
    c: Distance(g0) = 8
    c: Coincident(g1,g0)
    c: Vertical(g1)
    c: Distance(g1) = 3
    c: Coincident(g2,g0)
    c: Vertical(g2)
    c: Distance(g2) = 3
    c: Coincident(g3,g1)
    c: Horizontal(g3)
    c: Distance(g3) = 3
    c: Coincident(g4,g2)
    c: Horizontal(g4)
    c: Distance(g4) = 3
    c: Vertical(g5)
    c: Vertical(g6)
    c: Coincident(g7,g6)
    c: Coincident(g7,g5)
    c: Weight(g8) = 1
    c: Equal(g8,g9)
    c: Equal(g8,g10)
    c: Coincident(g11,g4)
    c: InternalAlignment(g8,g11)
    c: InternalAlignment(g9,g11)
    c: InternalAlignment(g10,g11)
    c: InternalAlignment(g12,g11)
    c: InternalAlignment(g13,g11)
    c: Coincident(g17,g5)
    c: Weight(g14) = 1
    c: Equal(g14,g15)
    c: Equal(g14,g16)
    c: Coincident(g17,g3)
    c: InternalAlignment(g14,g17)
    c: InternalAlignment(g15,g17)
    c: InternalAlignment(g16,g17)
    c: InternalAlignment(g18,g17)
    c: InternalAlignment(g19,g17)
    c: Block(g7)
    c: Block(g17)
    c: Block(g11)
    c: Block(g6)
FEATURE [Part::Extrusion] Extrude003
  Base = -> Sketch002
  Dir = (0,0,1)
  DirMode = 2
  FaceMakerClass = Part::FaceMakerBullseye
  LengthFwd = 260
  LengthRev = 0
  Solid = true
  Symmetric = false
FEATURE [Part::Extrusion] Extrude
  Base = -> Sketch
  Dir = (0,0,1)
  DirMode = 2
  FaceMakerClass = Part::FaceMakerBullseye
  LengthFwd = 14
  LengthRev = 0
  Solid = true
  Symmetric = false
